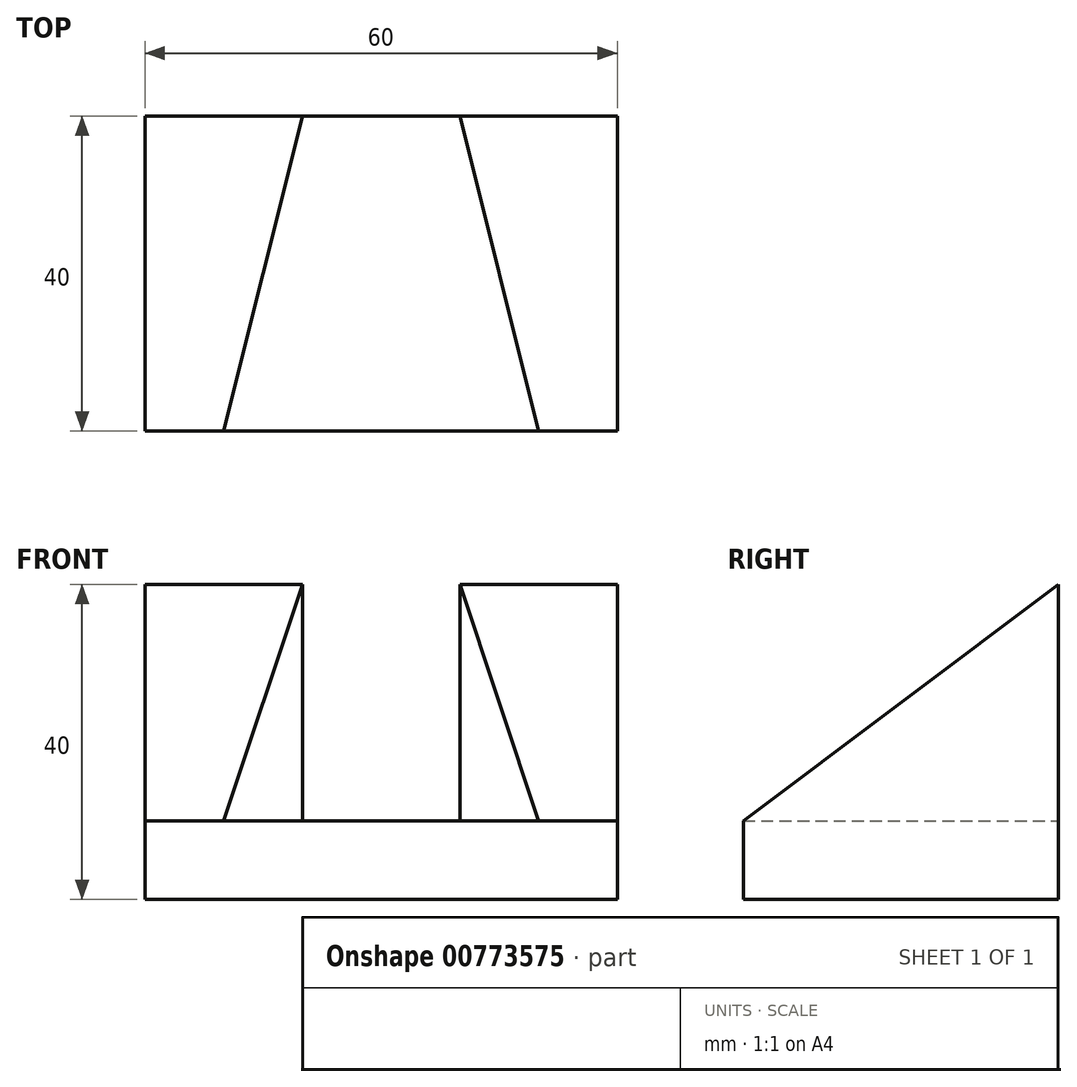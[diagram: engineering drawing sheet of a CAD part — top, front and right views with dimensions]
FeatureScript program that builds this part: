
annotation { "Feature Type Name" : "Feature", "Feature Type Description" : "" }
export const myFeature = defineFeature(function(context is Context, id is Id, definition is map)
    precondition{}
    {
        {
            var Q0;
            Q0=qCreatedBy(makeId("Top.planeOp"),FACE);
            var sketch = newSketch(context, id + "F0", { "sketchPlane" : qUnion([Q0])});
            skLineSegment(sketch, "E0.bottom", {"start": v(30, 20) * mm, "end": v(-30, 20) * mm});
            skLineSegment(sketch, "E0.top", {"start": v(30, -20) * mm, "end": v(-30, -20) * mm});
            skLineSegment(sketch, "E0.left", {"start": v(30, 20) * mm, "end": v(30, -20) * mm});
            skLineSegment(sketch, "E0.right", {"start": v(-30, 20) * mm, "end": v(-30, -20) * mm});
            skPoint(sketch, "E0.middle", {"position": v(0, 0) * mm});
            skSolve(sketch);
        }
        {
            var Q0;
            Q0=makeQuery(id+"F0.imprint","IMPRINT",FACE,{"disambiguationData":[TD([[makeQuery(id+"F0.imprint","IMPRINT",EDGE,{"derivedFrom":sQuery(id+"F0.wireOp",EDGE,"E0.bottom")}),1.0]])]});
            extrude(context, id + "F1", {"entities" : qUnion([Q0]), "depth" : 10 * mm, "offsetDistance" : 25 * mm});
        }
        {
            var Q0;
            Q0=makeQuery(id+"F1.opExtrude","SWEPT_FACE",FACE,{"disambiguationData":[OSD([sQuery(id+"F0.wireOp",EDGE,"E0.top")])]});
            var sketch = newSketch(context, id + "F2", { "sketchPlane" : qUnion([Q0])});
            skLineSegment(sketch, "E1.bottom", {"start": v(-30, 10) * mm, "end": v(-10, 10) * mm});
            skLineSegment(sketch, "E1.top", {"start": v(-30, 40) * mm, "end": v(-10, 40) * mm});
            skLineSegment(sketch, "E1.left", {"start": v(-30, 10) * mm, "end": v(-30, 40) * mm});
            skLineSegment(sketch, "E1.right", {"start": v(-10, 10) * mm, "end": v(-10, 40) * mm});
            skSolve(sketch);
        }
        {
            var Q0;
            Q0=makeQuery(id+"F2.imprint","IMPRINT",FACE,{"disambiguationData":[TD([[makeQuery(id+"F2.imprint","IMPRINT",EDGE,{"derivedFrom":sQuery(id+"F2.wireOp",EDGE,"E1.bottom")}),-1.0]])]});
            extrude(context, id + "F3", {"entities" : qUnion([Q0]), "operationType" : NewBodyOperationType.ADD, "oppositeDirection" : true, "depth" : 40 * mm, "offsetDistance" : 25 * mm});
        }
        {
            var Q0;
            Q0=makeQuery(id+"F3.opExtrude","SWEPT_FACE",FACE,{"disambiguationData":[OSD([sQuery(id+"F2.wireOp",EDGE,"E1.top")])]});
            var sketch = newSketch(context, id + "F4", { "sketchPlane" : qUnion([Q0])});
            skLineSegment(sketch, "E2", {"start": v(-10, -20) * mm, "end": v(-20, -20) * mm});
            skLineSegment(sketch, "E3", {"start": v(-20, -20) * mm, "end": v(-10, 20) * mm});
            skLineSegment(sketch, "E4", {"start": v(-10, 20) * mm, "end": v(-10, -20) * mm});
            skSolve(sketch);
        }
        {
            var Q0;
            Q0=makeQuery(id+"F4.imprint","IMPRINT",FACE,{"disambiguationData":[TD([[makeQuery(id+"F4.imprint","IMPRINT",EDGE,{"derivedFrom":sQuery(id+"F4.wireOp",EDGE,"E2")}),1.0]])]});
            extrude(context, id + "F5", {"entities" : qUnion([Q0]), "operationType" : NewBodyOperationType.REMOVE, "oppositeDirection" : true, "depth" : 30 * mm, "offsetDistance" : 25 * mm});
        }
        {
            var Q0;
            Q0=makeQuery(id+"F3.boolean.opBoolean","MERGE",FACE,{"derivedFrom":[makeQuery(id+"F1.opExtrude","SWEPT_FACE",FACE,{"disambiguationData":[OSD([sQuery(id+"F0.wireOp",EDGE,"E0.right")])]}),makeQuery(id+"F3.opExtrude","SWEPT_FACE",FACE,{"disambiguationData":[OSD([sQuery(id+"F2.wireOp",EDGE,"E1.left")])]})]});
            var sketch = newSketch(context, id + "F6", { "sketchPlane" : qUnion([Q0])});
            skLineSegment(sketch, "E5", {"start": v(-20, 40) * mm, "end": v(20, 40) * mm});
            skLineSegment(sketch, "E6", {"start": v(20, 40) * mm, "end": v(-20, 40) * mm});
            skLineSegment(sketch, "E7", {"start": v(20, 10) * mm, "end": v(-20, 40) * mm});
            skLineSegment(sketch, "E8", {"start": v(20, 10) * mm, "end": v(20, 40) * mm});
            skSolve(sketch);
        }
        {
            var Q0;
            Q0=makeQuery(id+"F6.imprint","IMPRINT",FACE,{"disambiguationData":[TD([[makeQuery(id+"F6.imprint","IMPRINT",EDGE,{"derivedFrom":sQuery(id+"F6.wireOp",EDGE,"E5")}),-1.0]])]});
            extrude(context, id + "F7", {"entities" : qUnion([Q0]), "operationType" : NewBodyOperationType.REMOVE, "oppositeDirection" : true, "depth" : 20 * mm, "offsetDistance" : 25 * mm});
        }
        {
            var Q0;
            Q0=makeQuery(id+"F5.boolean.opBoolean","MERGE",FACE,{"derivedFrom":[makeQuery(id+"F1.opExtrude","CAP_FACE",FACE,{"disambiguationData":[OSD([sQuery(id+"F0.wireOp",EDGE,"E0.bottom"),sQuery(id+"F0.wireOp",EDGE,"E0.top"),sQuery(id+"F0.wireOp",EDGE,"E0.left"),sQuery(id+"F0.wireOp",EDGE,"E0.right")])],"isStart":false}),makeQuery(id+"F5.opExtrude","CAP_FACE",FACE,{"disambiguationData":[OSD([sQuery(id+"F4.wireOp",EDGE,"E2"),sQuery(id+"F4.wireOp",EDGE,"E3"),sQuery(id+"F4.wireOp",EDGE,"E4")])],"isStart":false})]});
            var sketch = newSketch(context, id + "F8", { "sketchPlane" : qUnion([Q0])});
            skLineSegment(sketch, "E9.bottom", {"start": v(30, 20) * mm, "end": v(10, 20) * mm});
            skLineSegment(sketch, "E9.top", {"start": v(30, -20) * mm, "end": v(10, -20) * mm});
            skLineSegment(sketch, "E9.left", {"start": v(30, 20) * mm, "end": v(30, -20) * mm});
            skLineSegment(sketch, "E9.right", {"start": v(10, 20) * mm, "end": v(10, -20) * mm});
            skSolve(sketch);
        }
        {
            var Q0;
            Q0=makeQuery(id+"F8.imprint","IMPRINT",FACE,{"disambiguationData":[TD([[makeQuery(id+"F8.imprint","IMPRINT",EDGE,{"derivedFrom":sQuery(id+"F8.wireOp",EDGE,"E9.bottom")}),1.0]])]});
            extrude(context, id + "F9", {"entities" : qUnion([Q0]), "operationType" : NewBodyOperationType.ADD, "depth" : 30 * mm, "offsetDistance" : 25 * mm});
        }
        {
            var Q0;
            Q0=makeQuery(id+"F9.opExtrude","CAP_FACE",FACE,{"disambiguationData":[OSD([sQuery(id+"F8.wireOp",EDGE,"E9.bottom"),sQuery(id+"F8.wireOp",EDGE,"E9.top"),sQuery(id+"F8.wireOp",EDGE,"E9.left"),sQuery(id+"F8.wireOp",EDGE,"E9.right")])],"isStart":false});
            var sketch = newSketch(context, id + "F10", { "sketchPlane" : qUnion([Q0])});
            skLineSegment(sketch, "E10", {"start": v(20, -20) * mm, "end": v(10, 20) * mm});
            skLineSegment(sketch, "E11", {"start": v(10, 20) * mm, "end": v(10, -20) * mm});
            skLineSegment(sketch, "E12", {"start": v(10, -20) * mm, "end": v(20, -20) * mm});
            skSolve(sketch);
        }
        {
            var Q0;
            Q0=makeQuery(id+"F10.imprint","IMPRINT",FACE,{"disambiguationData":[TD([[makeQuery(id+"F10.imprint","IMPRINT",EDGE,{"derivedFrom":sQuery(id+"F10.wireOp",EDGE,"E10")}),1.0]])]});
            extrude(context, id + "F11", {"entities" : qUnion([Q0]), "operationType" : NewBodyOperationType.REMOVE, "oppositeDirection" : true, "depth" : 30 * mm, "offsetDistance" : 25 * mm});
        }
        {
            var Q0;
            Q0=makeQuery(id+"F9.boolean.opBoolean","MERGE",FACE,{"derivedFrom":[makeQuery(id+"F1.opExtrude","SWEPT_FACE",FACE,{"disambiguationData":[OSD([sQuery(id+"F0.wireOp",EDGE,"E0.left")])]}),makeQuery(id+"F9.opExtrude","SWEPT_FACE",FACE,{"disambiguationData":[OSD([sQuery(id+"F8.wireOp",EDGE,"E9.left")])]})]});
            var sketch = newSketch(context, id + "F12", { "sketchPlane" : qUnion([Q0])});
            skLineSegment(sketch, "E13", {"start": v(20, 40) * mm, "end": v(-20, 40) * mm});
            skLineSegment(sketch, "E14", {"start": v(-20, 40) * mm, "end": v(-20, 10) * mm});
            skLineSegment(sketch, "E15", {"start": v(-20, 10) * mm, "end": v(20, 40) * mm});
            skSolve(sketch);
        }
        {
            var Q0;
            Q0=makeQuery(id+"F12.imprint","IMPRINT",FACE,{"disambiguationData":[TD([[makeQuery(id+"F12.imprint","IMPRINT",EDGE,{"derivedFrom":sQuery(id+"F12.wireOp",EDGE,"E13")}),1.0]])]});
            extrude(context, id + "F13", {"entities" : qUnion([Q0]), "operationType" : NewBodyOperationType.REMOVE, "oppositeDirection" : true, "depth" : 20 * mm, "offsetDistance" : 25 * mm});
        }
    });
